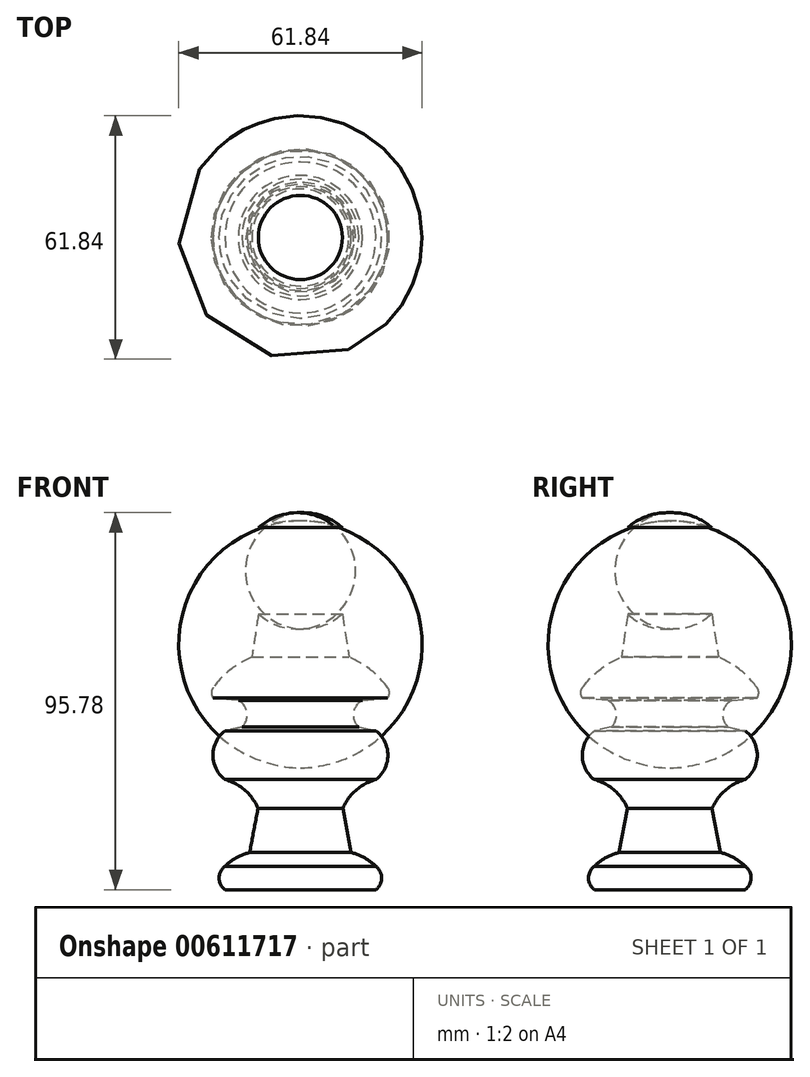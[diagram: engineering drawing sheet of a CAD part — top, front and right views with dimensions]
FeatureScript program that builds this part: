
annotation { "Feature Type Name" : "Feature", "Feature Type Description" : "" }
export const myFeature = defineFeature(function(context is Context, id is Id, definition is map)
    precondition{}
    {
        {
            var Q0;
            Q0=qCreatedBy(makeId("Front.planeOp"),FACE);
            var sketch = newSketch(context, id + "F0", { "sketchPlane" : qUnion([Q0])});
            skLineSegment(sketch, "E0", {"start": v(0, -58.39) * mm, "end": v(-19.17, -58.39) * mm});
            skArc(sketch, "E1", {"start": v(-19.17, -52.44) * mm, "mid": v(-20.65, -55.41) * mm, "end": v(-19.17, -58.39) * mm});
            skArc(sketch, "E2", {"start": v(-12.9, -48.97) * mm, "mid": v(-16.28, -50.27) * mm, "end": v(-19.17, -52.44) * mm});
            skLineSegment(sketch, "E3", {"start": v(-12.9, -48.97) * mm, "end": v(-10.76, -37.7) * mm});
            skArc(sketch, "E4", {"start": v(-10.76, -37.7) * mm, "mid": v(-14.15, -33.1) * mm, "end": v(-19.17, -30.4) * mm});
            skArc(sketch, "E5", {"start": v(-19.17, -18.04) * mm, "mid": v(-22.23, -24.22) * mm, "end": v(-19.17, -30.4) * mm});
            skLineSegment(sketch, "E6", {"start": v(-19.17, -18.04) * mm, "end": v(-14.83, -17.08) * mm});
            skArc(sketch, "E7", {"start": v(-14.83, -17.08) * mm, "mid": v(-13.58, -13.43) * mm, "end": v(-15.76, -10.26) * mm});
            skLineSegment(sketch, "E8", {"start": v(-15.76, -10.26) * mm, "end": v(-22.15, -9.72) * mm});
            skArc(sketch, "E9", {"start": v(-22.15, -7) * mm, "mid": v(-22.6, -8.36) * mm, "end": v(-22.15, -9.72) * mm});
            skArc(sketch, "E10", {"start": v(-12.32, 0.7) * mm, "mid": v(-17.76, -2.48) * mm, "end": v(-22.15, -7) * mm});
            skLineSegment(sketch, "E11", {"start": v(-12.32, 0.7) * mm, "end": v(-10.68, 11.61) * mm});
            skArc(sketch, "E12", {"start": v(-10.68, 33.58) * mm, "mid": v(-15.57, 22.6) * mm, "end": v(-10.68, 11.61) * mm});
            skArc(sketch, "E13", {"start": v(0, 35.3) * mm, "mid": v(-5.42, 34.9) * mm, "end": v(-10.68, 33.58) * mm});
            skLineSegment(sketch, "E14", {"start": v(0, 35.3) * mm, "end": v(0, -58.39) * mm});
            skSolve(sketch);
        }
        {
            var Q0;
            Q0 = qSketchRegion(id + "F0", true);
            var Q1;
            Q1=sQuery(id+"F0.wireOp",EDGE,"E13");
            var Q2;
            Q2=sQuery(id+"F0.wireOp",EDGE,"E12");
            var Q3;
            Q3=sQuery(id+"F0.wireOp",EDGE,"E11");
            var Q4;
            Q4=sQuery(id+"F0.wireOp",EDGE,"E10");
            var Q5;
            Q5=sQuery(id+"F0.wireOp",EDGE,"E9");
            var Q6;
            Q6=sQuery(id+"F0.wireOp",EDGE,"E8");
            var Q7;
            Q7=sQuery(id+"F0.wireOp",EDGE,"E7");
            var Q8;
            Q8=sQuery(id+"F0.wireOp",EDGE,"E6");
            var Q9;
            Q9=sQuery(id+"F0.wireOp",EDGE,"E5");
            var Q10;
            Q10=sQuery(id+"F0.wireOp",EDGE,"E4");
            var Q11;
            Q11=sQuery(id+"F0.wireOp",EDGE,"E3");
            var Q12;
            Q12=sQuery(id+"F0.wireOp",EDGE,"E2");
            var Q13;
            Q13=sQuery(id+"F0.wireOp",EDGE,"E1");
            var Q14;
            Q14=sQuery(id+"F0.wireOp",EDGE,"E0");
            var Q15;
            Q15=sQuery(id+"F0.wireOp",EDGE,"E14");
            revolve(context, id + "F1", {"bodyType" : ToolBodyType.SURFACE, "entities" : qUnion([Q0]), "surfaceEntities" : qUnion([Q1, Q2, Q3, Q4, Q5, Q6, Q7, Q8, Q9, Q10, Q11, Q12, Q13, Q14]), "axis" : qUnion([Q15]), "revolveType" : RevolveType.FULL});
        }
    });
